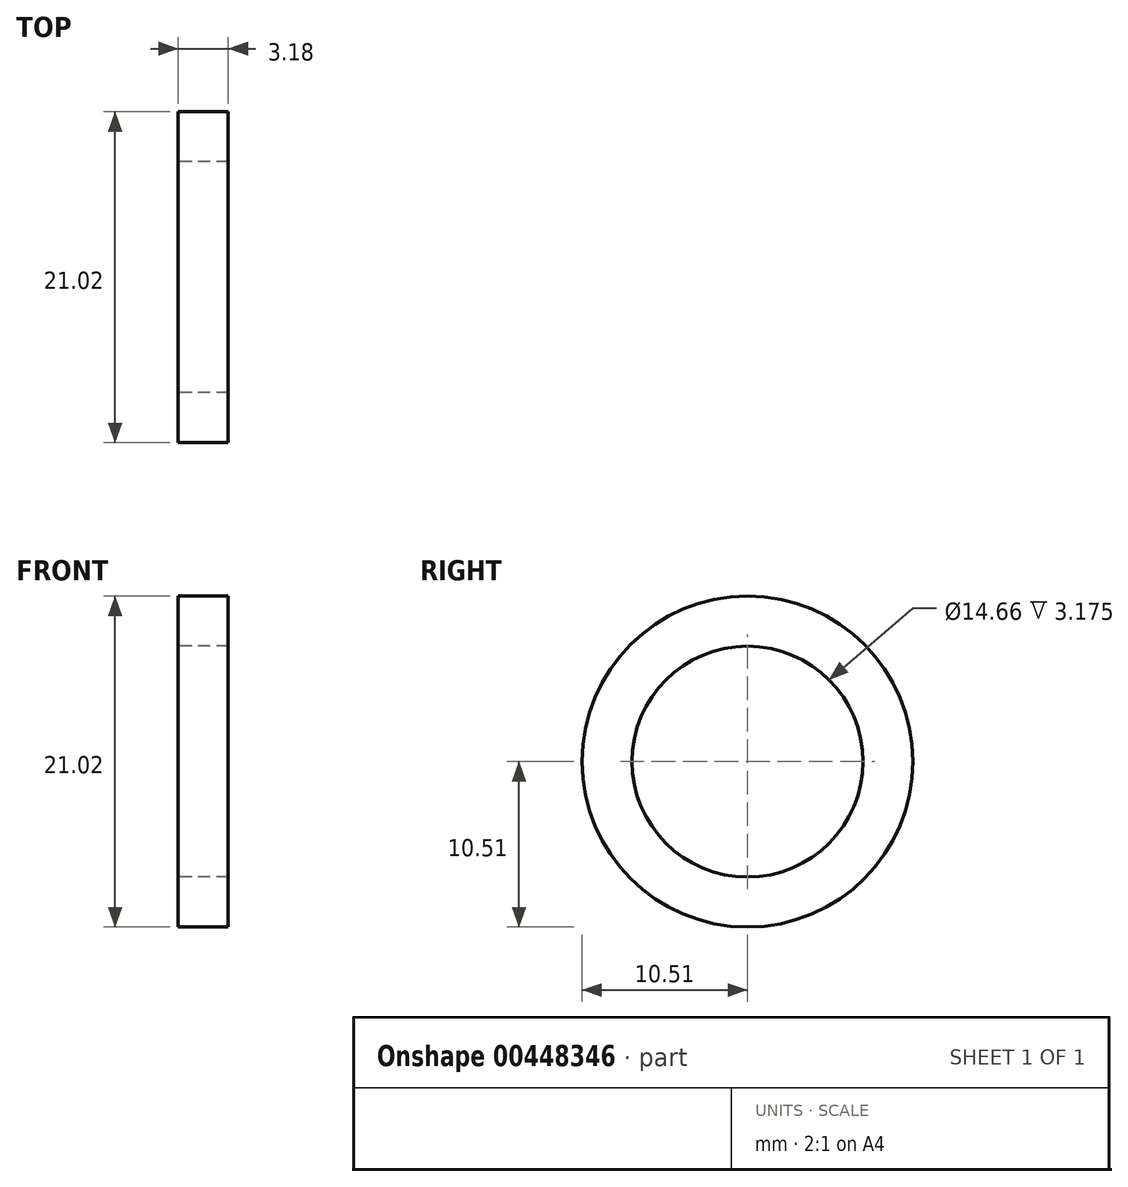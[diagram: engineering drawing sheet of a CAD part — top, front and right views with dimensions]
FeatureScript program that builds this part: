
annotation { "Feature Type Name" : "Feature", "Feature Type Description" : "" }
export const myFeature = defineFeature(function(context is Context, id is Id, definition is map)
    precondition{}
    {
        {
            var Q0;
            Q0=qCreatedBy(makeId("Right.planeOp"),FACE);
            var sketch = newSketch(context, id + "F0", { "sketchPlane" : qUnion([Q0])});
            skCircle(sketch, "E0", {"center": v(0, 0) * mm, "radius": 7.33 * mm});
            skCircle(sketch, "E1", {"center": v(0, 0) * mm, "radius": 10.5 * mm});
            skCircle(sketch, "E2.cCircle", {"center": v(0, 0) * mm, "radius": 6.35 * mm, "construction": true});
            skLineSegment(sketch, "E2.0", {"start": v(2.37, 6.94) * mm, "end": v(7.2, 1.41) * mm});
            skLineSegment(sketch, "E2.1", {"start": v(7.2, 1.41) * mm, "end": v(4.82, -5.52) * mm});
            skLineSegment(sketch, "E2.2", {"start": v(4.82, -5.52) * mm, "end": v(-2.37, -6.94) * mm});
            skLineSegment(sketch, "E2.3", {"start": v(-2.37, -6.94) * mm, "end": v(-7.2, -1.41) * mm});
            skLineSegment(sketch, "E2.4", {"start": v(-7.2, -1.41) * mm, "end": v(-4.82, 5.52) * mm});
            skLineSegment(sketch, "E2.5", {"start": v(-4.82, 5.52) * mm, "end": v(2.37, 6.94) * mm});
            skPoint(sketch, "E2.0.midPoint", {"position": v(4.78, 4.18) * mm});
            skSolve(sketch);
        }
        {
            var Q0;
            Q0=makeQuery(id+"F0.imprint","IMPRINT",FACE,{"disambiguationData":[TD([[makeQuery(id+"F0.imprint","IMPRINT",EDGE,{"derivedFrom":sQuery(id+"F0.wireOp",EDGE,"E1")}),1.0]])]});
            extrude(context, id + "F1", {"entities" : qUnion([Q0]), "depth" : 3.17 * mm});
        }
    });
